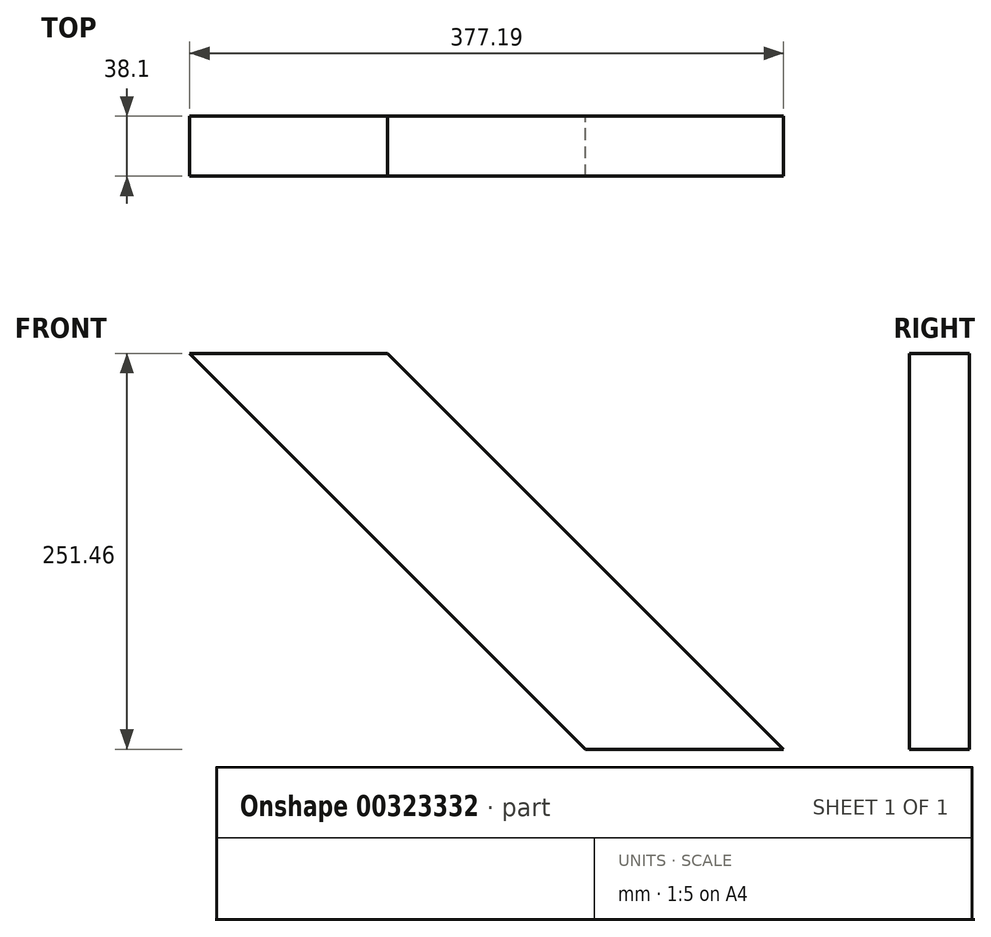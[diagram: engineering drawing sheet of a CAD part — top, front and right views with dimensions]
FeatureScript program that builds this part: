
annotation { "Feature Type Name" : "Feature", "Feature Type Description" : "" }
export const myFeature = defineFeature(function(context is Context, id is Id, definition is map)
    precondition{}
    {
        {
            var Q0;
            Q0=qCreatedBy(makeId("Front.planeOp"),FACE);
            var sketch = newSketch(context, id + "F0", { "sketchPlane" : qUnion([Q0])});
            skLineSegment(sketch, "E0", {"start": v(-227.41, 133.75) * mm, "end": v(-101.68, 133.75) * mm});
            skLineSegment(sketch, "E1", {"start": v(-101.68, 133.75) * mm, "end": v(149.78, -117.7) * mm});
            skLineSegment(sketch, "E2", {"start": v(149.78, -117.7) * mm, "end": v(24.05, -117.7) * mm});
            skLineSegment(sketch, "E3", {"start": v(24.05, -117.7) * mm, "end": v(-227.41, 133.75) * mm});
            skSolve(sketch);
        }
        {
            var Q0;
            Q0=makeQuery(id+"F0.imprint","IMPRINT",FACE,{"disambiguationData":[TD([[makeQuery(id+"F0.imprint","IMPRINT",EDGE,{"derivedFrom":sQuery(id+"F0.wireOp",EDGE,"E0")}),-1.0]])]});
            extrude(context, id + "F1", {"entities" : qUnion([Q0]), "depth" : 38.1 * mm});
        }
    });
